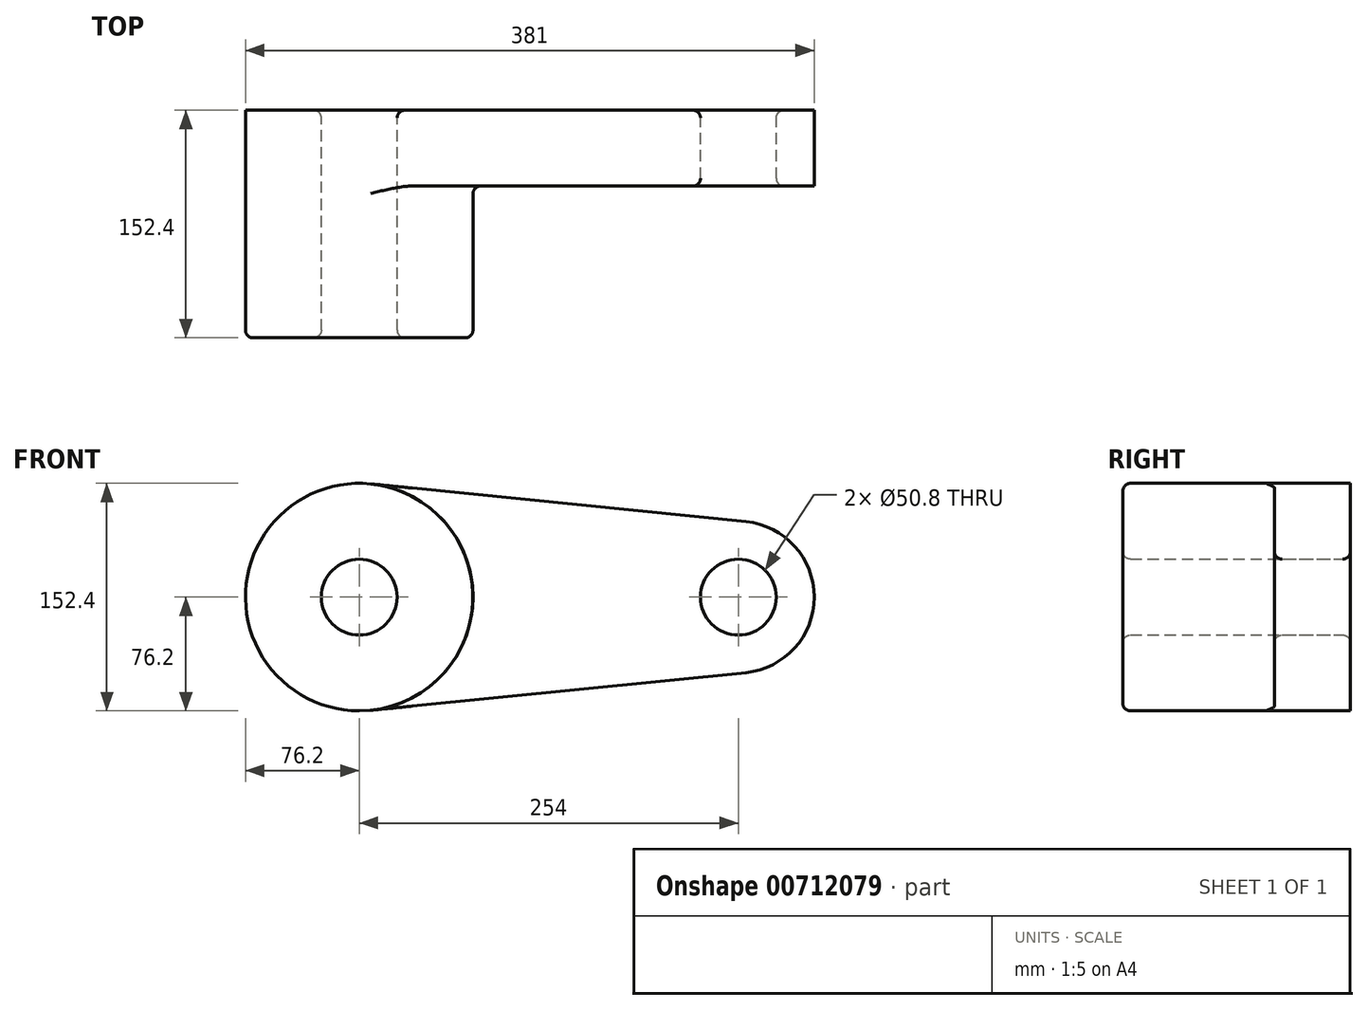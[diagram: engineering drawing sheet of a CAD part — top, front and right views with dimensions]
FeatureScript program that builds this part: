
annotation { "Feature Type Name" : "Feature", "Feature Type Description" : "" }
export const myFeature = defineFeature(function(context is Context, id is Id, definition is map)
    precondition{}
    {
        {
            var Q0;
            Q0=qCreatedBy(makeId("Front.planeOp"),FACE);
            var sketch = newSketch(context, id + "F0", { "sketchPlane" : qUnion([Q0])});
            skCircle(sketch, "E0", {"center": v(0, 0) * mm, "radius": 76.2 * mm});
            skCircle(sketch, "E1", {"center": v(254, 0) * mm, "radius": 50.8 * mm});
            skLineSegment(sketch, "E2", {"start": v(7.62, 75.82) * mm, "end": v(259.08, 50.55) * mm});
            skLineSegment(sketch, "E3", {"start": v(259.08, -50.55) * mm, "end": v(7.62, -75.82) * mm});
            skCircle(sketch, "E4", {"center": v(0, 0) * mm, "radius": 25.4 * mm});
            skCircle(sketch, "E5", {"center": v(254, 0) * mm, "radius": 25.4 * mm});
            skSolve(sketch);
        }
        {
            var Q0;
            Q0 = qSketchRegion(id + "F0", true);
            extrude(context, id + "F1", {"entities" : qUnion([Q0]), "depth" : 50.8 * mm, "offsetDistance" : 25.4 * mm});
        }
        {
            var Q0;
            Q0=makeQuery(id+"F0.imprint","IMPRINT",FACE,{"disambiguationData":[TD([[makeQuery(id+"F0.imprint","IMPRINT",EDGE,{"derivedFrom":sQuery(id+"F0.wireOp",EDGE,"E4")}),-1.0]])]});
            extrude(context, id + "F2", {"entities" : qUnion([Q0]), "operationType" : NewBodyOperationType.ADD, "depth" : 152.4 * mm, "offsetDistance" : 25.4 * mm});
        }
        {
            var Q0;
            {var subQ0=sQuery(id+"F0.wireOp",EDGE,"E4");Q0=makeQuery(id+"F2.boolean.opBoolean","MERGE",FACE,{"derivedFrom":[makeQuery(id+"F1.opExtrude","SWEPT_FACE",FACE,{"disambiguationData":[OSD([subQ0])]}),makeQuery(id+"F2.opExtrude","SWEPT_FACE",FACE,{"disambiguationData":[OSD([subQ0])]})]});}
            var Q1;
            Q1=makeQuery(id+"F2.opExtrude","CAP_EDGE",EDGE,{"disambiguationData":[OSD([sQuery(id+"F0.wireOp",EDGE,"E0")])],"isStart":false});
            var Q2;
            Q2=makeQuery(id+"F1.opExtrude","CAP_EDGE",EDGE,{"disambiguationData":[OSD([sQuery(id+"F0.wireOp",EDGE,"E5")])],"isStart":false});
            fillet(context, id + "F3", {"entities" : qUnion([Q0, Q1, Q2]), "radius" : 5.08 * mm, "tangentPropagation" : true, "allowEdgeOverflow" : false});
        }
        {
            var Q0;
            {var subQ0=sQuery(id+"F0.wireOp",EDGE,"E0");Q0=makeQuery(id+"F2.boolean.opBoolean","INTERSECT",EDGE,{"derivedFrom":[makeQuery(id+"F1.opExtrude","CAP_FACE",FACE,{"disambiguationData":[OSD([subQ0,sQuery(id+"F0.wireOp",EDGE,"E1"),sQuery(id+"F0.wireOp",EDGE,"E2"),sQuery(id+"F0.wireOp",EDGE,"E3"),sQuery(id+"F0.wireOp",EDGE,"E4"),sQuery(id+"F0.wireOp",EDGE,"E5")])],"isStart":false}),makeQuery(id+"F2.opExtrude","SWEPT_FACE",FACE,{"disambiguationData":[OSD([subQ0])]})]});}
            fillet(context, id + "F4", {"entities" : qUnion([Q0]), "radius" : 5.08 * mm, "tangentPropagation" : true, "allowEdgeOverflow" : false});
        }
        {
            var Q0;
            Q0=makeQuery(id+"F1.opExtrude","CAP_EDGE",EDGE,{"disambiguationData":[OSD([sQuery(id+"F0.wireOp",EDGE,"E5")])],"isStart":true});
            fillet(context, id + "F5", {"entities" : qUnion([Q0]), "radius" : 5.08 * mm, "tangentPropagation" : true, "allowEdgeOverflow" : false});
        }
    });
